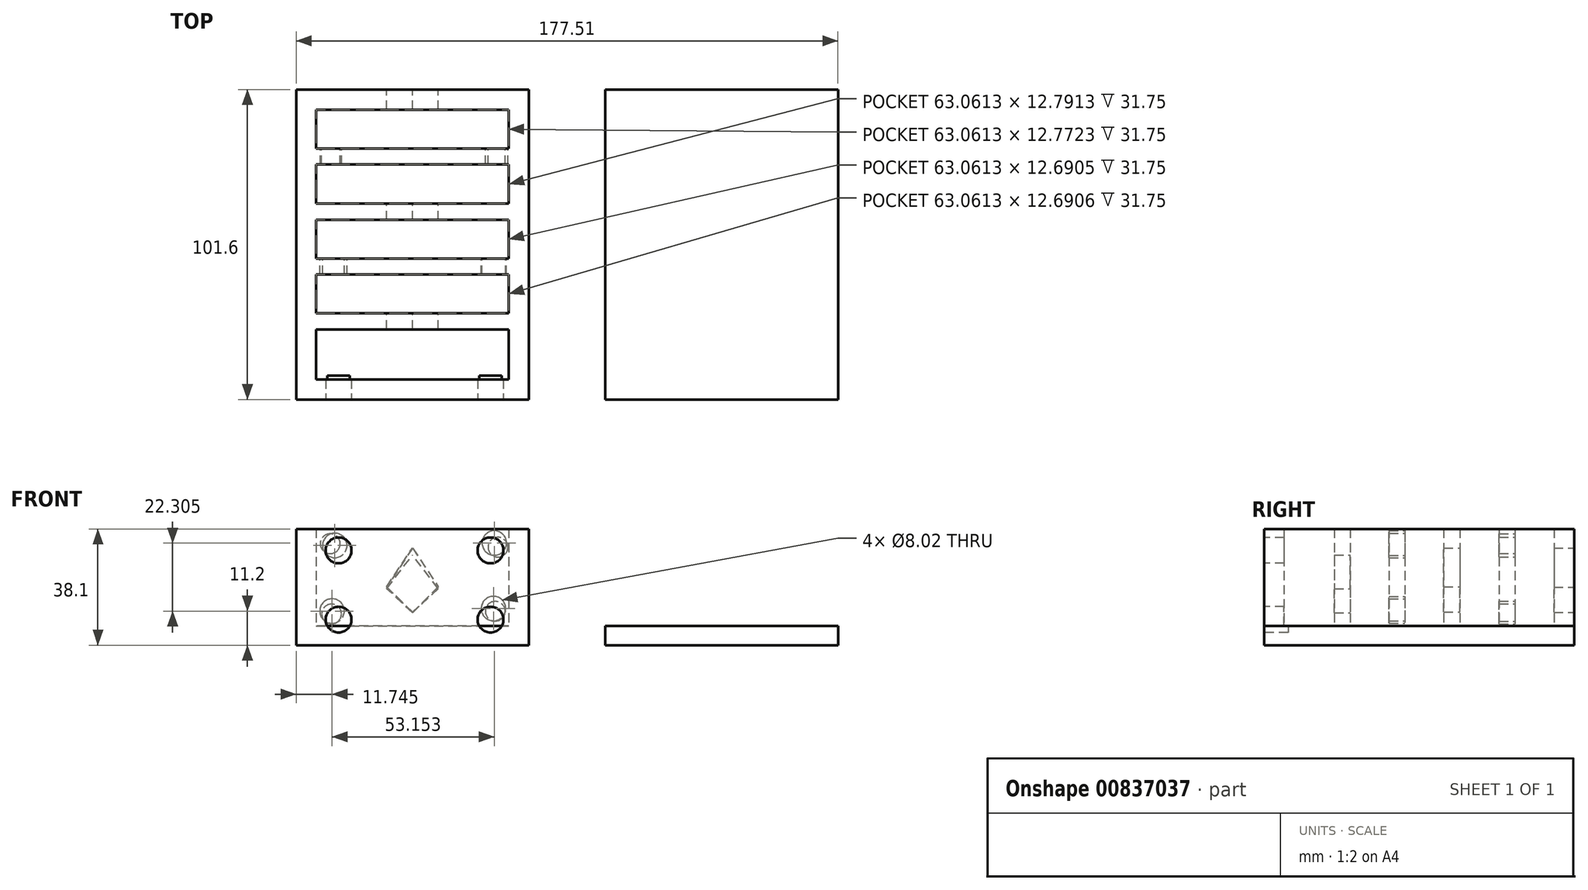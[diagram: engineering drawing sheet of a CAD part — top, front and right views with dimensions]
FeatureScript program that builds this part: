
annotation { "Feature Type Name" : "Feature", "Feature Type Description" : "" }
export const myFeature = defineFeature(function(context is Context, id is Id, definition is map)
    precondition{}
    {
        {
            var Q0;
            Q0=qCreatedBy(makeId("Top.planeOp"),FACE);
            var sketch = newSketch(context, id + "F0", { "sketchPlane" : qUnion([Q0])});
            skLineSegment(sketch, "E0.bottom", {"start": v(38.1, -50.8) * mm, "end": v(-38.1, -50.8) * mm});
            skLineSegment(sketch, "E0.top", {"start": v(38.1, 50.8) * mm, "end": v(-38.1, 50.8) * mm});
            skLineSegment(sketch, "E0.left", {"start": v(38.1, -50.8) * mm, "end": v(38.1, 50.8) * mm});
            skLineSegment(sketch, "E0.right", {"start": v(-38.1, -50.8) * mm, "end": v(-38.1, 50.8) * mm});
            skPoint(sketch, "E0.middle", {"position": v(0, 0) * mm});
            skLineSegment(sketch, "E1", {"start": v(-38.1, 50.8) * mm, "end": v(-31.53, 50.8) * mm});
            skLineSegment(sketch, "E2", {"start": v(-31.53, 50.8) * mm, "end": v(-31.53, -50.8) * mm});
            skLineSegment(sketch, "E3", {"start": v(-38.1, -50.8) * mm, "end": v(-38.1, -44.23) * mm});
            skLineSegment(sketch, "E4", {"start": v(-38.1, -44.23) * mm, "end": v(38.1, -44.23) * mm});
            skLineSegment(sketch, "E5", {"start": v(38.1, -50.8) * mm, "end": v(31.53, -50.8) * mm});
            skLineSegment(sketch, "E6", {"start": v(31.53, -50.8) * mm, "end": v(31.53, 50.8) * mm});
            skLineSegment(sketch, "E7", {"start": v(38.1, 50.8) * mm, "end": v(38.1, 44.22) * mm});
            skLineSegment(sketch, "E8", {"start": v(38.1, 44.22) * mm, "end": v(-38.1, 44.22) * mm});
            skLineSegment(sketch, "E9", {"start": v(-31.53, 44.22) * mm, "end": v(-31.53, 31.45) * mm});
            skLineSegment(sketch, "E10", {"start": v(-31.53, 31.45) * mm, "end": v(31.53, 31.45) * mm});
            skLineSegment(sketch, "E11", {"start": v(31.53, 31.45) * mm, "end": v(31.53, 26.2) * mm});
            skLineSegment(sketch, "E12", {"start": v(31.53, 26.2) * mm, "end": v(-31.53, 26.2) * mm});
            skLineSegment(sketch, "E13", {"start": v(-31.53, 26.2) * mm, "end": v(-31.53, 13.42) * mm});
            skLineSegment(sketch, "E14", {"start": v(-31.53, 13.42) * mm, "end": v(31.53, 13.42) * mm});
            skLineSegment(sketch, "E15", {"start": v(31.53, 13.42) * mm, "end": v(31.53, 8.08) * mm});
            skLineSegment(sketch, "E16", {"start": v(31.53, 8.08) * mm, "end": v(-31.53, 8.08) * mm});
            skLineSegment(sketch, "E17", {"start": v(-31.53, 8.08) * mm, "end": v(-31.53, -4.61) * mm});
            skLineSegment(sketch, "E18", {"start": v(-31.53, -4.61) * mm, "end": v(31.53, -4.61) * mm});
            skLineSegment(sketch, "E19", {"start": v(31.53, -4.61) * mm, "end": v(31.53, -9.85) * mm});
            skLineSegment(sketch, "E20", {"start": v(31.53, -9.85) * mm, "end": v(-31.53, -9.85) * mm});
            skLineSegment(sketch, "E21", {"start": v(-31.53, -9.85) * mm, "end": v(-31.53, -22.54) * mm});
            skLineSegment(sketch, "E22", {"start": v(-31.53, -22.54) * mm, "end": v(31.53, -22.54) * mm});
            skLineSegment(sketch, "E23", {"start": v(31.53, -22.54) * mm, "end": v(31.53, -27.78) * mm});
            skLineSegment(sketch, "E24", {"start": v(31.53, -27.78) * mm, "end": v(-31.53, -27.78) * mm});
            skLineSegment(sketch, "E25.bottom", {"start": v(139.41, -50.8) * mm, "end": v(63.21, -50.8) * mm});
            skLineSegment(sketch, "E25.top", {"start": v(139.41, 50.8) * mm, "end": v(63.21, 50.8) * mm});
            skLineSegment(sketch, "E25.left", {"start": v(139.41, -50.8) * mm, "end": v(139.41, 50.8) * mm});
            skLineSegment(sketch, "E25.right", {"start": v(63.21, -50.8) * mm, "end": v(63.21, 50.8) * mm});
            skSolve(sketch);
        }
        {
            var Q0;
            {var subQ0=sQuery(id+"F0.wireOp",EDGE,"E0.right");var subQ1=sQuery(id+"F0.wireOp",EDGE,"E0.bottom");var subQ2=makeQuery(id+"F0.imprint","INTERSECT",VERTEX,{"derivedFrom":[subQ1,subQ0]});Q0=makeQuery(id+"F0.imprint","IMPRINT",FACE,{"disambiguationData":[TD([[makeQuery(id+"F0.imprint","IMPRINT",EDGE,{"disambiguationData":[TD([[subQ2,1.0]])],"derivedFrom":subQ1}),-1.0]])]});}
            var Q1;
            {var subQ0=sQuery(id+"F0.wireOp",EDGE,"E6");var subQ1=sQuery(id+"F0.wireOp",EDGE,"E0.top");var subQ2=makeQuery(id+"F0.imprint","INTERSECT",VERTEX,{"derivedFrom":[subQ1,subQ0]});Q1=makeQuery(id+"F0.imprint","IMPRINT",FACE,{"disambiguationData":[TD([[makeQuery(id+"F0.imprint","IMPRINT",EDGE,{"disambiguationData":[TD([[subQ2,1.0]])],"derivedFrom":subQ1}),1.0]])]});}
            var Q2;
            {var subQ0=sQuery(id+"F0.wireOp",EDGE,"E6");var subQ1=sQuery(id+"F0.wireOp",EDGE,"E0.bottom");var subQ2=makeQuery(id+"F0.imprint","INTERSECT",VERTEX,{"derivedFrom":[subQ1,subQ0]});Q2=makeQuery(id+"F0.imprint","IMPRINT",FACE,{"disambiguationData":[TD([[makeQuery(id+"F0.imprint","IMPRINT",EDGE,{"disambiguationData":[TD([[subQ2,1.0]])],"derivedFrom":subQ1}),-1.0]])]});}
            var Q3;
            {var subQ0=sQuery(id+"F0.wireOp",EDGE,"E0.right");var subQ1=sQuery(id+"F0.wireOp",EDGE,"E0.top");var subQ2=makeQuery(id+"F0.imprint","INTERSECT",VERTEX,{"derivedFrom":[subQ1,subQ0]});Q3=makeQuery(id+"F0.imprint","IMPRINT",FACE,{"disambiguationData":[TD([[makeQuery(id+"F0.imprint","IMPRINT",EDGE,{"disambiguationData":[TD([[subQ2,1.0]])],"derivedFrom":subQ1}),1.0]])]});}
            var Q4;
            {var subQ0=sQuery(id+"F0.wireOp",EDGE,"E6");var subQ1=sQuery(id+"F0.wireOp",EDGE,"E0.bottom");var subQ2=makeQuery(id+"F0.imprint","INTERSECT",VERTEX,{"derivedFrom":[subQ1,subQ0]});Q4=makeQuery(id+"F0.imprint","IMPRINT",FACE,{"disambiguationData":[TD([[makeQuery(id+"F0.imprint","IMPRINT",EDGE,{"disambiguationData":[TD([[subQ2,-1.0]])],"derivedFrom":subQ1}),-1.0]])]});}
            var Q5;
            {var subQ0=sQuery(id+"F0.wireOp",EDGE,"E6");var subQ1=sQuery(id+"F0.wireOp",EDGE,"E0.top");var subQ2=makeQuery(id+"F0.imprint","INTERSECT",VERTEX,{"derivedFrom":[subQ1,subQ0]});Q5=makeQuery(id+"F0.imprint","IMPRINT",FACE,{"disambiguationData":[TD([[makeQuery(id+"F0.imprint","IMPRINT",EDGE,{"disambiguationData":[TD([[subQ2,-1.0]])],"derivedFrom":subQ1}),1.0]])]});}
            var Q6;
            {var subQ8=sQuery(id+"F0.wireOp",EDGE,"E4");var subQ9=sQuery(id+"F0.wireOp",EDGE,"E0.left");var subQ10=makeQuery(id+"F0.imprint","INTERSECT",VERTEX,{"derivedFrom":[subQ9,subQ8]});Q6=makeQuery(id+"F0.imprint","IMPRINT",FACE,{"disambiguationData":[TD([[makeQuery(id+"F0.imprint","IMPRINT",EDGE,{"disambiguationData":[TD([[subQ10,-1.0]])],"derivedFrom":subQ9}),1.0]])]});}
            var Q7;
            {var subQ8=sQuery(id+"F0.wireOp",EDGE,"E0.right");var subQ13=sQuery(id+"F0.wireOp",EDGE,"E4");var subQ14=makeQuery(id+"F0.imprint","INTERSECT",VERTEX,{"derivedFrom":[subQ8,subQ13]});Q7=makeQuery(id+"F0.imprint","IMPRINT",FACE,{"disambiguationData":[TD([[makeQuery(id+"F0.imprint","IMPRINT",EDGE,{"disambiguationData":[TD([[subQ14,-1.0]])],"derivedFrom":subQ8}),-1.0]])]});}
            var Q8;
            {var subQ0=sQuery(id+"F0.wireOp",EDGE,"E10");Q8=makeQuery(id+"F0.imprint","IMPRINT",FACE,{"disambiguationData":[TD([[makeQuery(id+"F0.imprint","IMPRINT",EDGE,{"derivedFrom":subQ0}),-1.0]])]});}
            var Q9;
            {var subQ0=sQuery(id+"F0.wireOp",EDGE,"E14");Q9=makeQuery(id+"F0.imprint","IMPRINT",FACE,{"disambiguationData":[TD([[makeQuery(id+"F0.imprint","IMPRINT",EDGE,{"derivedFrom":subQ0}),-1.0]])]});}
            var Q10;
            {var subQ0=sQuery(id+"F0.wireOp",EDGE,"E18");Q10=makeQuery(id+"F0.imprint","IMPRINT",FACE,{"disambiguationData":[TD([[makeQuery(id+"F0.imprint","IMPRINT",EDGE,{"derivedFrom":subQ0}),-1.0]])]});}
            var Q11;
            {var subQ2=sQuery(id+"F0.wireOp",EDGE,"E22");Q11=makeQuery(id+"F0.imprint","IMPRINT",FACE,{"disambiguationData":[TD([[makeQuery(id+"F0.imprint","IMPRINT",EDGE,{"derivedFrom":subQ2}),-1.0]])]});}
            extrude(context, id + "F1", {"entities" : qUnion([Q0, Q1, Q2, Q3, Q4, Q5, Q6, Q7, Q8, Q9, Q10, Q11]), "depth" : 38.1 * mm, "offsetDistance" : 25.4 * mm});
        }
        {
            var Q0;
            {var subQ0=sQuery(id+"F0.wireOp",EDGE,"E10");Q0=makeQuery(id+"F0.imprint","IMPRINT",FACE,{"disambiguationData":[TD([[makeQuery(id+"F0.imprint","IMPRINT",EDGE,{"derivedFrom":subQ0}),1.0]])]});}
            var Q1;
            {var subQ0=sQuery(id+"F0.wireOp",EDGE,"E12");Q1=makeQuery(id+"F0.imprint","IMPRINT",FACE,{"disambiguationData":[TD([[makeQuery(id+"F0.imprint","IMPRINT",EDGE,{"derivedFrom":subQ0}),1.0]])]});}
            var Q2;
            {var subQ0=sQuery(id+"F0.wireOp",EDGE,"E16");Q2=makeQuery(id+"F0.imprint","IMPRINT",FACE,{"disambiguationData":[TD([[makeQuery(id+"F0.imprint","IMPRINT",EDGE,{"derivedFrom":subQ0}),1.0]])]});}
            var Q3;
            {var subQ0=sQuery(id+"F0.wireOp",EDGE,"E20");Q3=makeQuery(id+"F0.imprint","IMPRINT",FACE,{"disambiguationData":[TD([[makeQuery(id+"F0.imprint","IMPRINT",EDGE,{"derivedFrom":subQ0}),1.0]])]});}
            var Q4;
            {var subQ0=sQuery(id+"F0.wireOp",EDGE,"E24");Q4=makeQuery(id+"F0.imprint","IMPRINT",FACE,{"disambiguationData":[TD([[makeQuery(id+"F0.imprint","IMPRINT",EDGE,{"derivedFrom":subQ0}),1.0]])]});}
            extrude(context, id + "F2", {"entities" : qUnion([Q0, Q1, Q2, Q3, Q4]), "operationType" : NewBodyOperationType.ADD, "depth" : 6.35 * mm, "offsetDistance" : 25.4 * mm});
        }
        {
            var Q0;
            Q0=makeQuery(id+"F1.opExtrude","SWEPT_FACE",FACE,{"disambiguationData":[OSD([sQuery(id+"F0.wireOp",EDGE,"E0.top")])]});
            var sketch = newSketch(context, id + "F3", { "sketchPlane" : qUnion([Q0])});
            skLineSegment(sketch, "E26", {"start": v(0, 38.1) * mm, "end": v(0, 0) * mm});
            skLineSegment(sketch, "E27", {"start": v(0, 19.05) * mm, "end": v(8.45, 19.05) * mm});
            skLineSegment(sketch, "E28", {"start": v(8.45, 19.05) * mm, "end": v(0, 31.87) * mm});
            skLineSegment(sketch, "E29", {"start": v(0, 19.05) * mm, "end": v(-8.46, 19.05) * mm});
            skLineSegment(sketch, "E30", {"start": v(-8.46, 19.05) * mm, "end": v(0, 31.87) * mm});
            skLineSegment(sketch, "E31", {"start": v(-8.46, 19.05) * mm, "end": v(0, 10.7) * mm});
            skLineSegment(sketch, "E32", {"start": v(0, 10.7) * mm, "end": v(8.45, 19.05) * mm});
            skSolve(sketch);
        }
        {
            var Q0;
            {var subQ0=sQuery(id+"F3.wireOp",EDGE,"E27");Q0=makeQuery(id+"F3.imprint","IMPRINT",FACE,{"disambiguationData":[TD([[makeQuery(id+"F3.imprint","IMPRINT",EDGE,{"derivedFrom":subQ0}),1.0]])]});}
            var Q1;
            {var subQ0=sQuery(id+"F3.wireOp",EDGE,"E29");Q1=makeQuery(id+"F3.imprint","IMPRINT",FACE,{"disambiguationData":[TD([[makeQuery(id+"F3.imprint","IMPRINT",EDGE,{"derivedFrom":subQ0}),-1.0]])]});}
            var Q2;
            {var subQ0=sQuery(id+"F3.wireOp",EDGE,"E27");Q2=makeQuery(id+"F3.imprint","IMPRINT",FACE,{"disambiguationData":[TD([[makeQuery(id+"F3.imprint","IMPRINT",EDGE,{"derivedFrom":subQ0}),-1.0]])]});}
            var Q3;
            {var subQ0=sQuery(id+"F3.wireOp",EDGE,"E29");Q3=makeQuery(id+"F3.imprint","IMPRINT",FACE,{"disambiguationData":[TD([[makeQuery(id+"F3.imprint","IMPRINT",EDGE,{"derivedFrom":subQ0}),1.0]])]});}
            extrude(context, id + "F4", {"entities" : qUnion([Q0, Q1, Q2, Q3]), "operationType" : NewBodyOperationType.REMOVE, "oppositeDirection" : true, "depth" : 12.7 * mm, "offsetDistance" : 25.4 * mm});
        }
        {
            var Q0;
            Q0=makeQuery(id+"F1.opExtrude","SWEPT_FACE",FACE,{"disambiguationData":[OSD([sQuery(id+"F0.wireOp",EDGE,"E10")])]});
            var sketch = newSketch(context, id + "F5", { "sketchPlane" : qUnion([Q0])});
            skCircle(sketch, "E33", {"center": v(-27.1, 11.14) * mm, "radius": 3.25 * mm});
            skCircle(sketch, "E34", {"center": v(-28, 32.14) * mm, "radius": 3.25 * mm});
            skCircle(sketch, "E35", {"center": v(26.96, 33.26) * mm, "radius": 3.25 * mm});
            skCircle(sketch, "E36", {"center": v(26.51, 10.25) * mm, "radius": 3.25 * mm});
            skSolve(sketch);
        }
        {
            var Q0;
            Q0=makeQuery(id+"F5.imprint","IMPRINT",FACE,{"disambiguationData":[TD([[makeQuery(id+"F5.imprint","IMPRINT",EDGE,{"derivedFrom":sQuery(id+"F5.wireOp",EDGE,"E33")}),1.0]])]});
            var Q1;
            Q1=makeQuery(id+"F5.imprint","IMPRINT",FACE,{"disambiguationData":[TD([[makeQuery(id+"F5.imprint","IMPRINT",EDGE,{"derivedFrom":sQuery(id+"F5.wireOp",EDGE,"E34")}),1.0]])]});
            var Q2;
            Q2=makeQuery(id+"F5.imprint","IMPRINT",FACE,{"disambiguationData":[TD([[makeQuery(id+"F5.imprint","IMPRINT",EDGE,{"derivedFrom":sQuery(id+"F5.wireOp",EDGE,"E35")}),1.0]])]});
            var Q3;
            Q3=makeQuery(id+"F5.imprint","IMPRINT",FACE,{"disambiguationData":[TD([[makeQuery(id+"F5.imprint","IMPRINT",EDGE,{"derivedFrom":sQuery(id+"F5.wireOp",EDGE,"E36")}),1.0]])]});
            extrude(context, id + "F6", {"entities" : qUnion([Q0, Q1, Q2, Q3]), "operationType" : NewBodyOperationType.REMOVE, "oppositeDirection" : true, "depth" : 7.62 * mm, "offsetDistance" : 25.4 * mm});
        }
        {
            var Q0;
            Q0=makeQuery(id+"F1.opExtrude","SWEPT_FACE",FACE,{"disambiguationData":[OSD([sQuery(id+"F0.wireOp",EDGE,"E14")])]});
            var sketch = newSketch(context, id + "F7", { "sketchPlane" : qUnion([Q0])});
            skLineSegment(sketch, "E37", {"start": v(0, 6.35) * mm, "end": v(0, 34.8) * mm});
            skLineSegment(sketch, "E38", {"start": v(0, 19.16) * mm, "end": v(8.45, 19.16) * mm});
            skLineSegment(sketch, "E39", {"start": v(0, 19.16) * mm, "end": v(-8.46, 19.16) * mm});
            skLineSegment(sketch, "E40", {"start": v(0, 19.16) * mm, "end": v(0, 10.85) * mm});
            skLineSegment(sketch, "E41", {"start": v(0, 10.85) * mm, "end": v(8.45, 19.16) * mm});
            skLineSegment(sketch, "E42", {"start": v(-8.46, 19.16) * mm, "end": v(0, 10.85) * mm});
            skLineSegment(sketch, "E43", {"start": v(8.45, 19.16) * mm, "end": v(0, 31.83) * mm});
            skLineSegment(sketch, "E44", {"start": v(0, 31.83) * mm, "end": v(-8.46, 19.16) * mm});
            skSolve(sketch);
        }
        {
            var Q0;
            {var subQ0=sQuery(id+"F7.wireOp",EDGE,"E39");Q0=makeQuery(id+"F7.imprint","IMPRINT",FACE,{"disambiguationData":[TD([[makeQuery(id+"F7.imprint","IMPRINT",EDGE,{"derivedFrom":subQ0}),-1.0]])]});}
            var Q1;
            Q1=makeQuery(id+"F7.imprint","IMPRINT",FACE,{"disambiguationData":[TD([[makeQuery(id+"F7.imprint","IMPRINT",EDGE,{"derivedFrom":sQuery(id+"F7.wireOp",EDGE,"E39")}),1.0]])]});
            var Q2;
            {var subQ0=sQuery(id+"F7.wireOp",EDGE,"E38");Q2=makeQuery(id+"F7.imprint","IMPRINT",FACE,{"disambiguationData":[TD([[makeQuery(id+"F7.imprint","IMPRINT",EDGE,{"derivedFrom":subQ0}),1.0]])]});}
            var Q3;
            Q3=makeQuery(id+"F7.imprint","IMPRINT",FACE,{"disambiguationData":[TD([[makeQuery(id+"F7.imprint","IMPRINT",EDGE,{"derivedFrom":sQuery(id+"F7.wireOp",EDGE,"E38")}),-1.0]])]});
            extrude(context, id + "F8", {"entities" : qUnion([Q0, Q1, Q2, Q3]), "operationType" : NewBodyOperationType.REMOVE, "oppositeDirection" : true, "depth" : 7.62 * mm, "offsetDistance" : 25.4 * mm});
        }
        {
            var Q0;
            Q0=makeQuery(id+"F1.opExtrude","SWEPT_FACE",FACE,{"disambiguationData":[OSD([sQuery(id+"F0.wireOp",EDGE,"E18")])]});
            var sketch = newSketch(context, id + "F9", { "sketchPlane" : qUnion([Q0])});
            skCircle(sketch, "E45", {"center": v(-26.53, 12) * mm, "radius": 4.01 * mm});
            skCircle(sketch, "E46", {"center": v(-26.8, 33.5) * mm, "radius": 4.01 * mm});
            skCircle(sketch, "E47", {"center": v(25.46, 32.7) * mm, "radius": 4.01 * mm});
            skCircle(sketch, "E48", {"center": v(26.36, 11.2) * mm, "radius": 4.01 * mm});
            skSolve(sketch);
        }
        {
            var Q0;
            Q0=makeQuery(id+"F9.imprint","IMPRINT",FACE,{"disambiguationData":[TD([[makeQuery(id+"F9.imprint","IMPRINT",EDGE,{"derivedFrom":sQuery(id+"F9.wireOp",EDGE,"E45")}),1.0]])]});
            var Q1;
            Q1=makeQuery(id+"F9.imprint","IMPRINT",FACE,{"disambiguationData":[TD([[makeQuery(id+"F9.imprint","IMPRINT",EDGE,{"derivedFrom":sQuery(id+"F9.wireOp",EDGE,"E46")}),1.0]])]});
            var Q2;
            Q2=makeQuery(id+"F9.imprint","IMPRINT",FACE,{"disambiguationData":[TD([[makeQuery(id+"F9.imprint","IMPRINT",EDGE,{"derivedFrom":sQuery(id+"F9.wireOp",EDGE,"E48")}),1.0]])]});
            var Q3;
            Q3=makeQuery(id+"F9.imprint","IMPRINT",FACE,{"disambiguationData":[TD([[makeQuery(id+"F9.imprint","IMPRINT",EDGE,{"derivedFrom":sQuery(id+"F9.wireOp",EDGE,"E47")}),1.0]])]});
            extrude(context, id + "F10", {"entities" : qUnion([Q0, Q1, Q2, Q3]), "operationType" : NewBodyOperationType.REMOVE, "oppositeDirection" : true, "depth" : 7.62 * mm, "offsetDistance" : 25.4 * mm});
        }
        {
            var Q0;
            Q0=makeQuery(id+"F1.opExtrude","SWEPT_FACE",FACE,{"disambiguationData":[OSD([sQuery(id+"F0.wireOp",EDGE,"E22")])]});
            var sketch = newSketch(context, id + "F11", { "sketchPlane" : qUnion([Q0])});
            skLineSegment(sketch, "E49", {"start": v(0, 6.35) * mm, "end": v(0, 33.48) * mm});
            skLineSegment(sketch, "E50", {"start": v(0, 18.55) * mm, "end": v(8.46, 18.55) * mm});
            skLineSegment(sketch, "E51", {"start": v(8.46, 18.55) * mm, "end": v(0, 29.52) * mm});
            skLineSegment(sketch, "E52", {"start": v(0, 18.55) * mm, "end": v(-8.47, 18.55) * mm});
            skLineSegment(sketch, "E53", {"start": v(-8.47, 18.55) * mm, "end": v(0, 29.52) * mm});
            skLineSegment(sketch, "E54", {"start": v(-8.47, 18.55) * mm, "end": v(0, 10.68) * mm});
            skLineSegment(sketch, "E55", {"start": v(0, 10.68) * mm, "end": v(8.46, 18.55) * mm});
            skSolve(sketch);
        }
        {
            var Q0;
            {var subQ0=sQuery(id+"F11.wireOp",EDGE,"E52");Q0=makeQuery(id+"F11.imprint","IMPRINT",FACE,{"disambiguationData":[TD([[makeQuery(id+"F11.imprint","IMPRINT",EDGE,{"derivedFrom":subQ0}),1.0]])]});}
            var Q1;
            {var subQ0=sQuery(id+"F11.wireOp",EDGE,"E50");Q1=makeQuery(id+"F11.imprint","IMPRINT",FACE,{"disambiguationData":[TD([[makeQuery(id+"F11.imprint","IMPRINT",EDGE,{"derivedFrom":subQ0}),-1.0]])]});}
            var Q2;
            {var subQ0=sQuery(id+"F11.wireOp",EDGE,"E50");Q2=makeQuery(id+"F11.imprint","IMPRINT",FACE,{"disambiguationData":[TD([[makeQuery(id+"F11.imprint","IMPRINT",EDGE,{"derivedFrom":subQ0}),1.0]])]});}
            var Q3;
            {var subQ0=sQuery(id+"F11.wireOp",EDGE,"E52");Q3=makeQuery(id+"F11.imprint","IMPRINT",FACE,{"disambiguationData":[TD([[makeQuery(id+"F11.imprint","IMPRINT",EDGE,{"derivedFrom":subQ0}),-1.0]])]});}
            extrude(context, id + "F12", {"entities" : qUnion([Q0, Q1, Q2, Q3]), "operationType" : NewBodyOperationType.REMOVE, "oppositeDirection" : true, "depth" : 7.62 * mm, "offsetDistance" : 25.4 * mm});
        }
        {
            var Q0;
            Q0=makeQuery(id+"F1.opExtrude","SWEPT_FACE",FACE,{"disambiguationData":[OSD([sQuery(id+"F0.wireOp",EDGE,"E0.bottom")])]});
            var sketch = newSketch(context, id + "F13", { "sketchPlane" : qUnion([Q0])});
            skCircle(sketch, "E56", {"center": v(-24.21, 31.07) * mm, "radius": 4.23 * mm});
            skCircle(sketch, "E57", {"center": v(-24.21, 8.39) * mm, "radius": 4.23 * mm});
            skCircle(sketch, "E58", {"center": v(25.56, 8.39) * mm, "radius": 4.23 * mm});
            skCircle(sketch, "E59", {"center": v(25.56, 31.07) * mm, "radius": 4.23 * mm});
            skSolve(sketch);
        }
        {
            var Q0;
            Q0=makeQuery(id+"F13.imprint","IMPRINT",FACE,{"disambiguationData":[TD([[makeQuery(id+"F13.imprint","IMPRINT",EDGE,{"derivedFrom":sQuery(id+"F13.wireOp",EDGE,"E57")}),1.0]])]});
            var Q1;
            Q1=makeQuery(id+"F13.imprint","IMPRINT",FACE,{"disambiguationData":[TD([[makeQuery(id+"F13.imprint","IMPRINT",EDGE,{"derivedFrom":sQuery(id+"F13.wireOp",EDGE,"E56")}),1.0]])]});
            var Q2;
            Q2=makeQuery(id+"F13.imprint","IMPRINT",FACE,{"disambiguationData":[TD([[makeQuery(id+"F13.imprint","IMPRINT",EDGE,{"derivedFrom":sQuery(id+"F13.wireOp",EDGE,"E59")}),1.0]])]});
            var Q3;
            Q3=makeQuery(id+"F13.imprint","IMPRINT",FACE,{"disambiguationData":[TD([[makeQuery(id+"F13.imprint","IMPRINT",EDGE,{"derivedFrom":sQuery(id+"F13.wireOp",EDGE,"E58")}),1.0]])]});
            extrude(context, id + "F14", {"entities" : qUnion([Q0, Q1, Q2, Q3]), "operationType" : NewBodyOperationType.REMOVE, "oppositeDirection" : true, "depth" : 7.87 * mm, "offsetDistance" : 25.4 * mm});
        }
        {
            var Q0;
            Q0=makeQuery(id+"F0.imprint","IMPRINT",FACE,{"disambiguationData":[TD([[makeQuery(id+"F0.imprint","IMPRINT",EDGE,{"derivedFrom":sQuery(id+"F0.wireOp",EDGE,"E25.bottom")}),-1.0]])]});
            extrude(context, id + "F15", {"entities" : qUnion([Q0]), "depth" : 6.35 * mm, "offsetDistance" : 25.4 * mm});
        }
    });
